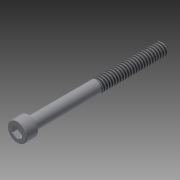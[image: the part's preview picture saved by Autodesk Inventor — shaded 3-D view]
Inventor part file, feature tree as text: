
AUTODESK INVENTOR PART (.ipt)
format: ipt  version: 2014 SP2 (Build 180246200, 246)  size: 110,592 bytes
history: native  units: in
note: dims shown in document units (in); Inventor stores cm internally (conversion verified against a paired STEP export)
features: other x7, sketch x2, revolve x1, thread x1, extrude x1
ambient origin geometry x8: Origin, YZ Plane, XZ Plane, XY Plane, X Axis, Y Axis, Z Axis, Center Point
bodies: Solid1 (feature_tree)
feature tree (12):
  revolve  "Revolution1"  [1 undecoded]
  thread  "Thread1"  [1 undecoded]
  extrude  "Extrusion1"  [1 undecoded]
  other  "screw_XY"
  other  "screw_YZ"
  other  "screw_ZX"
  other  "screw_X"
  other  "screw_Y"
  other  "screw_Z"
  other  "screw_Center"
  sketch  "Sketch_1"  dims[d0=360.0deg d1=0.6101in d2=0.0in d3=0.051in d4=0.0in]
  sketch  "Sketch_3"  dims[d5=0.0in]
note: 3 required parameter values undecoded (feature->parameter linkage not recoverable at this tier; creation-order binding heuristic only, values carry confidence <= 0.55)